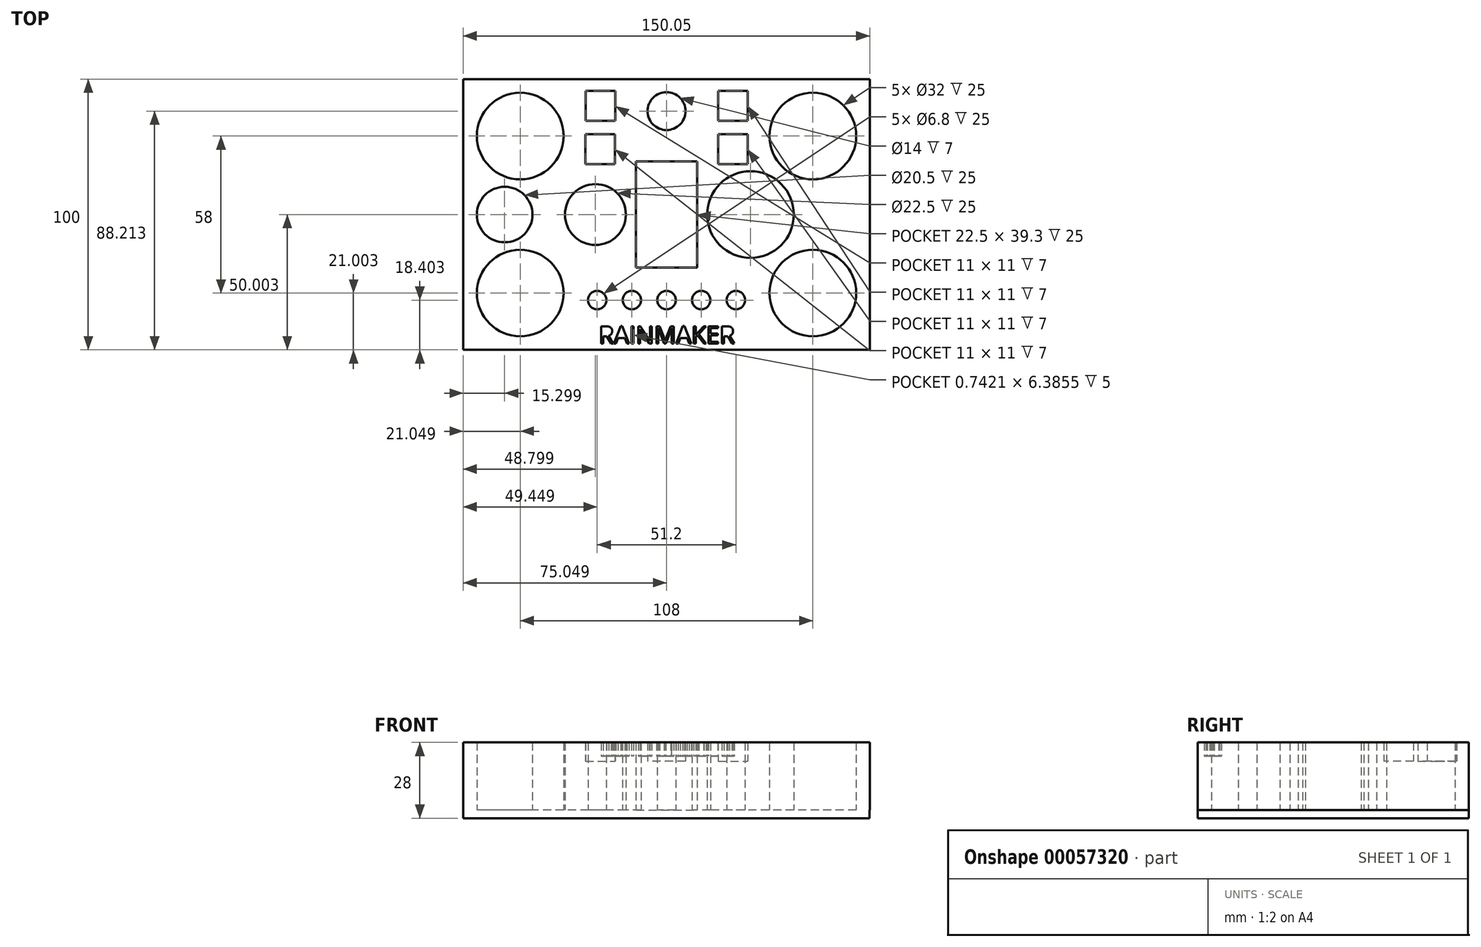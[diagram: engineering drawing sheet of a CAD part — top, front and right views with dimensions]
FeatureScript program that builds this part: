
annotation { "Feature Type Name" : "Feature", "Feature Type Description" : "" }
export const myFeature = defineFeature(function(context is Context, id is Id, definition is map)
    precondition{}
    {
        {
            var Q0;
            Q0=qCreatedBy(makeId("Top.planeOp"),FACE);
            var sketch = newSketch(context, id + "F0", { "sketchPlane" : qUnion([Q0])});
            skLineSegment(sketch, "E0.bottom", {"start": v(-74.95, 50.06) * mm, "end": v(75.05, 50.06) * mm});
            skLineSegment(sketch, "E0.top", {"start": v(-74.95, -49.94) * mm, "end": v(75.05, -49.94) * mm});
            skLineSegment(sketch, "E0.left", {"start": v(-74.95, 50.06) * mm, "end": v(-74.95, -49.94) * mm});
            skLineSegment(sketch, "E0.right", {"start": v(75.05, 50.06) * mm, "end": v(75.05, -49.94) * mm});
            skLineSegment(sketch, "E1.bottom", {"start": v(-11.2, 19.71) * mm, "end": v(11.3, 19.71) * mm});
            skLineSegment(sketch, "E1.top", {"start": v(-11.2, -19.59) * mm, "end": v(11.3, -19.59) * mm});
            skLineSegment(sketch, "E1.left", {"start": v(-11.2, 19.71) * mm, "end": v(-11.2, -19.59) * mm});
            skLineSegment(sketch, "E1.right", {"start": v(11.3, 19.71) * mm, "end": v(11.3, -19.59) * mm});
            skCircle(sketch, "E2", {"center": v(-53.95, 29.06) * mm, "radius": 16 * mm});
            skCircle(sketch, "E3", {"center": v(54.05, 29.06) * mm, "radius": 16 * mm});
            skCircle(sketch, "E4", {"center": v(-53.95, -28.94) * mm, "radius": 16 * mm});
            skCircle(sketch, "E5", {"center": v(54.05, -28.94) * mm, "radius": 16 * mm});
            skCircle(sketch, "E6", {"center": v(-59.7, 0.06) * mm, "radius": 10.25 * mm});
            skCircle(sketch, "E7", {"center": v(-26.2, 0.06) * mm, "radius": 11.25 * mm});
            skCircle(sketch, "E8", {"center": v(0.05, 38.27) * mm, "radius": 7 * mm});
            skLineSegment(sketch, "E9.bottom", {"start": v(-29.83, 45.7) * mm, "end": v(-18.83, 45.7) * mm});
            skLineSegment(sketch, "E9.top", {"start": v(-29.83, 34.7) * mm, "end": v(-18.83, 34.7) * mm});
            skLineSegment(sketch, "E9.left", {"start": v(-29.83, 45.7) * mm, "end": v(-29.83, 34.7) * mm});
            skLineSegment(sketch, "E9.right", {"start": v(-18.83, 45.7) * mm, "end": v(-18.83, 34.7) * mm});
            skLineSegment(sketch, "E10.top", {"start": v(19.05, 34.7) * mm, "end": v(30.05, 34.7) * mm});
            skLineSegment(sketch, "E10.left", {"start": v(19.05, 45.7) * mm, "end": v(19.05, 34.7) * mm});
            skLineSegment(sketch, "E10.bottom", {"start": v(19.05, 45.7) * mm, "end": v(30.05, 45.7) * mm});
            skLineSegment(sketch, "E10.right", {"start": v(30.05, 45.7) * mm, "end": v(30.05, 34.7) * mm});
            skLineSegment(sketch, "E11.top", {"start": v(19.05, 18.7) * mm, "end": v(30.05, 18.7) * mm});
            skLineSegment(sketch, "E11.left", {"start": v(19.05, 29.7) * mm, "end": v(19.05, 18.7) * mm});
            skLineSegment(sketch, "E11.bottom", {"start": v(19.05, 29.7) * mm, "end": v(30.05, 29.7) * mm});
            skLineSegment(sketch, "E11.right", {"start": v(30.05, 29.7) * mm, "end": v(30.05, 18.7) * mm});
            skLineSegment(sketch, "E12.top", {"start": v(-29.95, 18.7) * mm, "end": v(-18.95, 18.7) * mm});
            skLineSegment(sketch, "E12.left", {"start": v(-29.95, 29.7) * mm, "end": v(-29.95, 18.7) * mm});
            skLineSegment(sketch, "E12.bottom", {"start": v(-29.95, 29.7) * mm, "end": v(-18.95, 29.7) * mm});
            skLineSegment(sketch, "E12.right", {"start": v(-18.95, 29.7) * mm, "end": v(-18.95, 18.7) * mm});
            skCircle(sketch, "E13", {"center": v(31.05, 0.06) * mm, "radius": 16 * mm});
            skCircle(sketch, "E14", {"center": v(0.05, -31.54) * mm, "radius": 3.4 * mm});
            skCircle(sketch, "E15", {"center": v(12.85, -31.54) * mm, "radius": 3.4 * mm});
            skCircle(sketch, "E16", {"center": v(25.65, -31.54) * mm, "radius": 3.4 * mm});
            skCircle(sketch, "E17", {"center": v(-12.75, -31.54) * mm, "radius": 3.4 * mm});
            skCircle(sketch, "E18", {"center": v(-25.55, -31.54) * mm, "radius": 3.4 * mm});
            skText(sketch, "E19", { "text": "RAINMAKER", "fontName": "OpenSans-Regular.ttf"});
            const initialGuessF0  = {"E19": [-0.02495, -0.0476, 1, 0, 0.00644]};
            skSetInitialGuess(sketch, initialGuessF0);
            skSolve(sketch);
        }
        {
            var Q0;
            Q0=makeQuery(id+"F0.imprint","IMPRINT",FACE,{"disambiguationData":[TD([[makeQuery(id+"F0.imprint","IMPRINT",EDGE,{"derivedFrom":sQuery(id+"F0.wireOp",EDGE,"E0.bottom")}),-1.0]])]});
            extrude(context, id + "F1", {"entities" : qUnion([Q0]), "depth" : 25 * mm});
        }
        {
            var Q0;
            Q0=qCreatedBy(makeId("Right.planeOp"),FACE);
            var sketch = newSketch(context, id + "F2", { "sketchPlane" : qUnion([Q0])});
            skLineSegment(sketch, "E20.bottom", {"start": v(50.06, 0) * mm, "end": v(-49.94, 0) * mm});
            skLineSegment(sketch, "E20.top", {"start": v(50.06, -3) * mm, "end": v(-49.94, -3) * mm});
            skLineSegment(sketch, "E20.left", {"start": v(50.06, 0) * mm, "end": v(50.06, -3) * mm});
            skLineSegment(sketch, "E20.right", {"start": v(-49.94, 0) * mm, "end": v(-49.94, -3) * mm});
            skSolve(sketch);
        }
        {
            var Q0;
            Q0=makeQuery(id+"F2.imprint","IMPRINT",FACE,{"disambiguationData":[TD([[makeQuery(id+"F2.imprint","IMPRINT",EDGE,{"derivedFrom":sQuery(id+"F2.wireOp",EDGE,"E20.bottom")}),1.0]])]});
            extrude(context, id + "F3", {"entities" : qUnion([Q0]), "operationType" : NewBodyOperationType.ADD, "depth" : 75 * mm});
        }
        {
            var Q0;
            Q0=makeQuery(id+"F3.opExtrude","CAP_FACE",FACE,{"disambiguationData":[OSD([sQuery(id+"F2.wireOp",EDGE,"E20.bottom"),sQuery(id+"F2.wireOp",EDGE,"E20.top"),sQuery(id+"F2.wireOp",EDGE,"E20.left"),sQuery(id+"F2.wireOp",EDGE,"E20.right")])],"isStart":true});
            extrude(context, id + "F4", {"entities" : qUnion([Q0]), "operationType" : NewBodyOperationType.ADD, "depth" : 75 * mm});
        }
        {
            var Q0;
            Q0=makeQuery(id+"F4.boolean.opBoolean","SPLIT",FACE,{"disambiguationData":[TD([makeQuery(id+"F1.opExtrude","SWEPT_FACE",FACE,{"disambiguationData":[OSD([sQuery(id+"F0.wireOp",EDGE,"E9.bottom")])]})])],"derivedFrom":makeQuery(id+"F4.opExtrude","SWEPT_FACE",FACE,{"disambiguationData":[OSD([sQuery(id+"F2.wireOp",EDGE,"E20.bottom")])]})});
            extrude(context, id + "F5", {"entities" : qUnion([Q0]), "operationType" : NewBodyOperationType.ADD, "depth" : 18 * mm});
        }
        {
            var Q0;
            Q0=makeQuery(id+"F4.boolean.opBoolean","SPLIT",FACE,{"disambiguationData":[TD([makeQuery(id+"F1.opExtrude","SWEPT_FACE",FACE,{"disambiguationData":[OSD([sQuery(id+"F0.wireOp",EDGE,"E12.top")])]})])],"derivedFrom":makeQuery(id+"F4.opExtrude","SWEPT_FACE",FACE,{"disambiguationData":[OSD([sQuery(id+"F2.wireOp",EDGE,"E20.bottom")])]})});
            var Q1;
            Q1=makeQuery(id+"F3.boolean.opBoolean","SPLIT",FACE,{"disambiguationData":[TD([makeQuery(id+"F1.opExtrude","SWEPT_FACE",FACE,{"disambiguationData":[OSD([sQuery(id+"F0.wireOp",EDGE,"E11.top")])]})])],"derivedFrom":makeQuery(id+"F3.opExtrude","SWEPT_FACE",FACE,{"disambiguationData":[OSD([sQuery(id+"F2.wireOp",EDGE,"E20.bottom")])]})});
            var Q2;
            Q2=makeQuery(id+"F3.boolean.opBoolean","SPLIT",FACE,{"disambiguationData":[TD([makeQuery(id+"F1.opExtrude","SWEPT_FACE",FACE,{"disambiguationData":[OSD([sQuery(id+"F0.wireOp",EDGE,"E10.top")])]})])],"derivedFrom":makeQuery(id+"F3.opExtrude","SWEPT_FACE",FACE,{"disambiguationData":[OSD([sQuery(id+"F2.wireOp",EDGE,"E20.bottom")])]})});
            extrude(context, id + "F6", {"entities" : qUnion([Q0, Q1, Q2]), "operationType" : NewBodyOperationType.ADD, "depth" : 18 * mm});
        }
        {
            var Q0;
            {var subQ0=sQuery(id+"F2.wireOp",EDGE,"E20.bottom");var subQ1=sQuery(id+"F0.wireOp",EDGE,"E8");Q0=makeQuery(id+"F4.boolean.opBoolean","MERGE",FACE,{"derivedFrom":[makeQuery(id+"F3.boolean.opBoolean","SPLIT",FACE,{"disambiguationData":[TD([makeQuery(id+"F1.opExtrude","SWEPT_FACE",FACE,{"disambiguationData":[OSD([subQ1])]})])],"derivedFrom":makeQuery(id+"F3.opExtrude","SWEPT_FACE",FACE,{"disambiguationData":[OSD([subQ0])]})}),makeQuery(id+"F4.opExtrude","SWEPT_FACE",FACE,{"disambiguationData":[OSD([subQ0])]})]});}
            extrude(context, id + "F7", {"entities" : qUnion([Q0]), "operationType" : NewBodyOperationType.ADD, "depth" : 18 * mm});
        }
        {
            var Q0;
            Q0=makeQuery(id+"F4.boolean.opBoolean","SPLIT",FACE,{"disambiguationData":[TD([makeQuery(id+"F1.opExtrude","SWEPT_FACE",FACE,{"disambiguationData":[OSD([sQuery(id+"F0.wireOp",EDGE,"E19.sketch_text.stroke-18")])]})])],"derivedFrom":makeQuery(id+"F4.opExtrude","SWEPT_FACE",FACE,{"disambiguationData":[OSD([sQuery(id+"F2.wireOp",EDGE,"E20.bottom")])]})});
            var Q1;
            Q1=makeQuery(id+"F4.boolean.opBoolean","SPLIT",FACE,{"disambiguationData":[TD([makeQuery(id+"F1.opExtrude","SWEPT_FACE",FACE,{"disambiguationData":[OSD([sQuery(id+"F0.wireOp",EDGE,"E19.sketch_text.stroke-0")])]})])],"derivedFrom":makeQuery(id+"F4.opExtrude","SWEPT_FACE",FACE,{"disambiguationData":[OSD([sQuery(id+"F2.wireOp",EDGE,"E20.bottom")])]})});
            var Q2;
            Q2=makeQuery(id+"F4.boolean.opBoolean","SPLIT",FACE,{"disambiguationData":[TD([makeQuery(id+"F1.opExtrude","SWEPT_FACE",FACE,{"disambiguationData":[OSD([sQuery(id+"F0.wireOp",EDGE,"E19.sketch_text.stroke-31")])]})])],"derivedFrom":makeQuery(id+"F4.opExtrude","SWEPT_FACE",FACE,{"disambiguationData":[OSD([sQuery(id+"F2.wireOp",EDGE,"E20.bottom")])]})});
            var Q3;
            Q3=makeQuery(id+"F4.boolean.opBoolean","SPLIT",FACE,{"disambiguationData":[TD([makeQuery(id+"F1.opExtrude","SWEPT_FACE",FACE,{"disambiguationData":[OSD([sQuery(id+"F0.wireOp",EDGE,"E19.sketch_text.stroke-35")])]})])],"derivedFrom":makeQuery(id+"F4.opExtrude","SWEPT_FACE",FACE,{"disambiguationData":[OSD([sQuery(id+"F2.wireOp",EDGE,"E20.bottom")])]})});
            var Q4;
            {var subQ0=sQuery(id+"F2.wireOp",EDGE,"E20.bottom");var subQ4=sQuery(id+"F0.wireOp",EDGE,"E19.sketch_text.stroke-59");Q4=makeQuery(id+"F4.boolean.opBoolean","MERGE",FACE,{"derivedFrom":[makeQuery(id+"F3.boolean.opBoolean","SPLIT",FACE,{"disambiguationData":[TD([makeQuery(id+"F1.opExtrude","SWEPT_FACE",FACE,{"disambiguationData":[OSD([subQ4])]})])],"derivedFrom":makeQuery(id+"F3.opExtrude","SWEPT_FACE",FACE,{"disambiguationData":[OSD([subQ0])]})}),makeQuery(id+"F4.opExtrude","SWEPT_FACE",FACE,{"disambiguationData":[OSD([subQ0])]})]});}
            var Q5;
            Q5=makeQuery(id+"F3.boolean.opBoolean","SPLIT",FACE,{"disambiguationData":[TD([makeQuery(id+"F1.opExtrude","SWEPT_FACE",FACE,{"disambiguationData":[OSD([sQuery(id+"F0.wireOp",EDGE,"E19.sketch_text.stroke-68")])]})])],"derivedFrom":makeQuery(id+"F3.opExtrude","SWEPT_FACE",FACE,{"disambiguationData":[OSD([sQuery(id+"F2.wireOp",EDGE,"E20.bottom")])]})});
            var Q6;
            Q6=makeQuery(id+"F3.boolean.opBoolean","SPLIT",FACE,{"disambiguationData":[TD([makeQuery(id+"F1.opExtrude","SWEPT_FACE",FACE,{"disambiguationData":[OSD([sQuery(id+"F0.wireOp",EDGE,"E19.sketch_text.stroke-81")])]})])],"derivedFrom":makeQuery(id+"F3.opExtrude","SWEPT_FACE",FACE,{"disambiguationData":[OSD([sQuery(id+"F2.wireOp",EDGE,"E20.bottom")])]})});
            var Q7;
            Q7=makeQuery(id+"F3.boolean.opBoolean","SPLIT",FACE,{"disambiguationData":[TD([makeQuery(id+"F1.opExtrude","SWEPT_FACE",FACE,{"disambiguationData":[OSD([sQuery(id+"F0.wireOp",EDGE,"E19.sketch_text.stroke-105")])]})])],"derivedFrom":makeQuery(id+"F3.opExtrude","SWEPT_FACE",FACE,{"disambiguationData":[OSD([sQuery(id+"F2.wireOp",EDGE,"E20.bottom")])]})});
            var Q8;
            Q8=makeQuery(id+"F3.boolean.opBoolean","SPLIT",FACE,{"disambiguationData":[TD([makeQuery(id+"F1.opExtrude","SWEPT_FACE",FACE,{"disambiguationData":[OSD([sQuery(id+"F0.wireOp",EDGE,"E19.sketch_text.stroke-93")])]})])],"derivedFrom":makeQuery(id+"F3.opExtrude","SWEPT_FACE",FACE,{"disambiguationData":[OSD([sQuery(id+"F2.wireOp",EDGE,"E20.bottom")])]})});
            extrude(context, id + "F8", {"entities" : qUnion([Q0, Q1, Q2, Q3, Q4, Q5, Q6, Q7, Q8]), "operationType" : NewBodyOperationType.ADD, "depth" : 20 * mm});
        }
    });
